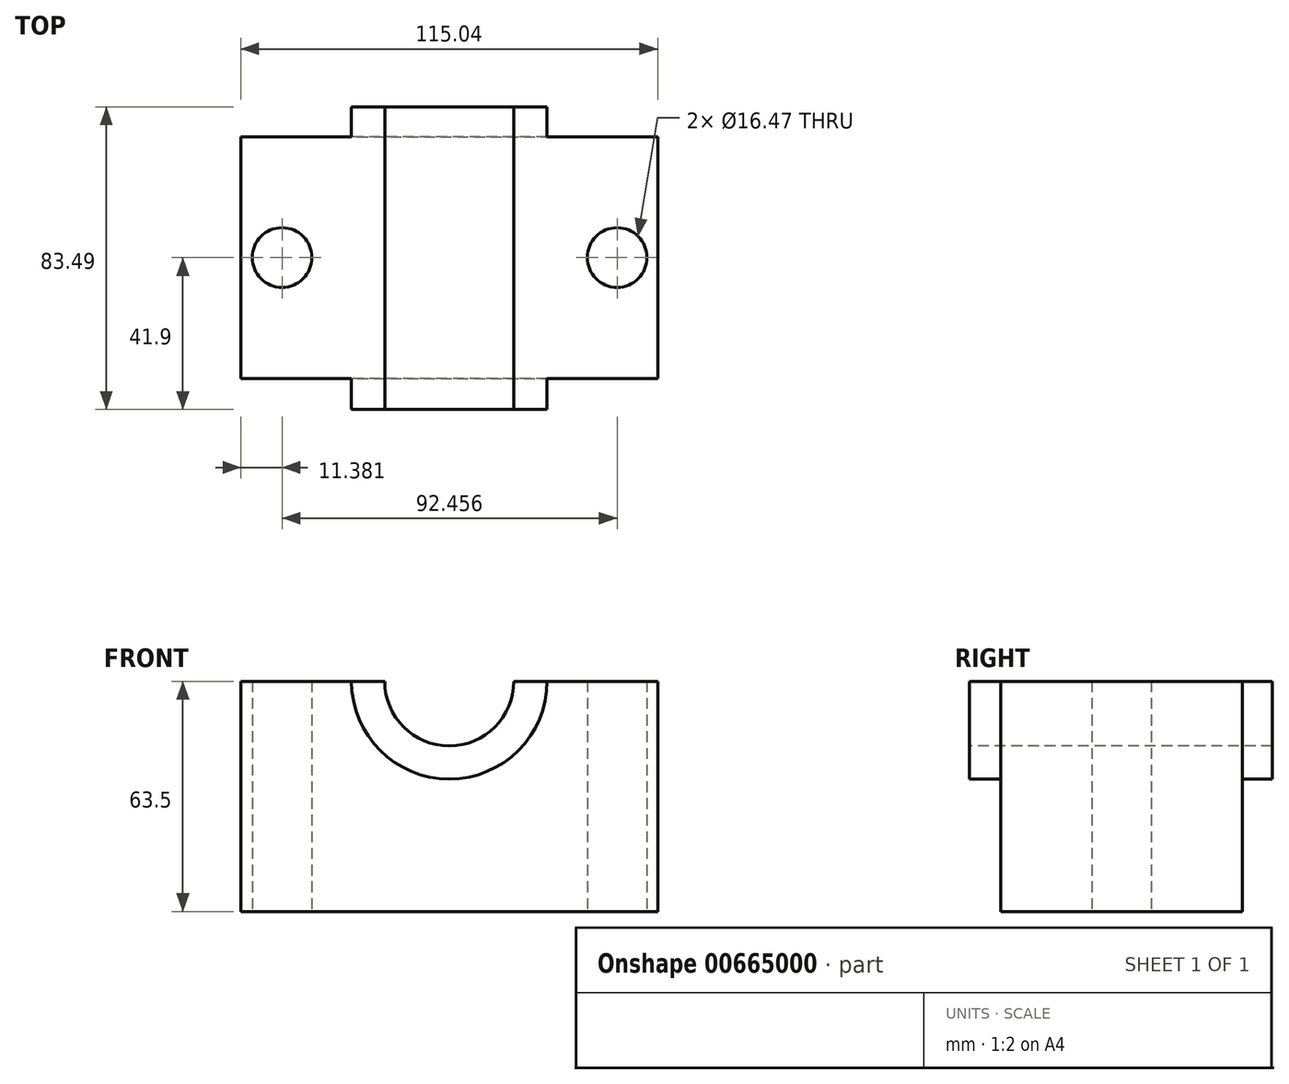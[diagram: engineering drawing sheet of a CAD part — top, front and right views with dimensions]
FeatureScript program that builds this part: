
annotation { "Feature Type Name" : "Feature", "Feature Type Description" : "" }
export const myFeature = defineFeature(function(context is Context, id is Id, definition is map)
    precondition{}
    {
        {
            var Q0;
            Q0=qCreatedBy(makeId("Top.planeOp"),FACE);
            var sketch = newSketch(context, id + "F0", { "sketchPlane" : qUnion([Q0])});
            skLineSegment(sketch, "E0.bottom", {"start": v(-57.52, 33.34) * mm, "end": v(57.52, 33.34) * mm});
            skLineSegment(sketch, "E0.top", {"start": v(-57.52, -33.34) * mm, "end": v(57.52, -33.34) * mm});
            skLineSegment(sketch, "E0.left", {"start": v(-57.52, 33.34) * mm, "end": v(-57.52, -33.34) * mm});
            skLineSegment(sketch, "E0.right", {"start": v(57.52, 33.34) * mm, "end": v(57.52, -33.34) * mm});
            skPoint(sketch, "E0.middle", {"position": v(0, 0) * mm});
            skCircle(sketch, "E1", {"center": v(-46.14, 0) * mm, "radius": 8.24 * mm});
            skCircle(sketch, "E2", {"center": v(46.32, 0) * mm, "radius": 8.24 * mm});
            skSolve(sketch);
        }
        {
            var Q0;
            Q0=makeQuery(id+"F0.imprint","IMPRINT",FACE,{"disambiguationData":[TD([[makeQuery(id+"F0.imprint","IMPRINT",EDGE,{"derivedFrom":sQuery(id+"F0.wireOp",EDGE,"E0.bottom")}),-1.0]])]});
            extrude(context, id + "F1", {"entities" : qUnion([Q0]), "depth" : 63.5 * mm, "offsetDistance" : 25.4 * mm});
        }
        {
            var Q0;
            Q0=makeQuery(id+"F1.opExtrude","SWEPT_FACE",FACE,{"disambiguationData":[OSD([sQuery(id+"F0.wireOp",EDGE,"E0.top")])]});
            var sketch = newSketch(context, id + "F2", { "sketchPlane" : qUnion([Q0])});
            skArc(sketch, "E3", {"start": v(-17.81, 63.5) * mm, "mid": v(0, 45.69) * mm, "end": v(17.81, 63.5) * mm});
            skLineSegment(sketch, "E4", {"start": v(-57.52, 63.5) * mm, "end": v(57.52, 63.5) * mm});
            skSolve(sketch);
        }
        {
            var Q0;
            {var subQ0=sQuery(id+"F2.wireOp",EDGE,"E3");var subQ1=makeQuery(id+"F1.opExtrude","CAP_EDGE",EDGE,{"disambiguationData":[OSD([sQuery(id+"F0.wireOp",EDGE,"E0.top")])],"isStart":false});var subQ2=makeQuery(id+"F2.imprint","INTERSECT",VERTEX,{"disambiguationData":[OD(0.0)],"derivedFrom":[subQ1,subQ0]});Q0=makeQuery(id+"F2.imprint","IMPRINT",FACE,{"disambiguationData":[TD([[makeQuery(id+"F2.imprint","IMPRINT",EDGE,{"disambiguationData":[TD([[subQ2,-1.0]])],"derivedFrom":subQ0}),1.0]])]});}
            extrude(context, id + "F3", {"entities" : qUnion([Q0]), "operationType" : NewBodyOperationType.REMOVE, "oppositeDirection" : true, "depth" : 76.2 * mm, "offsetDistance" : 25.4 * mm});
        }
        {
            var Q0;
            Q0=makeQuery(id+"F1.opExtrude","SWEPT_FACE",FACE,{"disambiguationData":[OSD([sQuery(id+"F0.wireOp",EDGE,"E0.top")])]});
            var sketch = newSketch(context, id + "F4", { "sketchPlane" : qUnion([Q0])});
            skArc(sketch, "E5", {"start": v(-26.98, 63.5) * mm, "mid": v(0, 36.52) * mm, "end": v(26.98, 63.5) * mm});
            skSolve(sketch);
        }
        {
            var Q0;
            Q0 = qSketchRegion(id + "F4", true);
            var Q1;
            {var subQ0=sQuery(id+"F4.wireOp",EDGE,"E5");Q1=makeQuery(id+"F4.imprint","IMPRINT",FACE,{"disambiguationData":[TD([[makeQuery(id+"F4.imprint","IMPRINT",EDGE,{"derivedFrom":subQ0}),1.0]])]});}
            extrude(context, id + "F5", {"entities" : qUnion([Q0, Q1]), "operationType" : NewBodyOperationType.ADD, "endBound" : BoundingType.SYMMETRIC, "depth" : 149.86 * mm, "offsetDistance" : 25.4 * mm});
        }
        {
            var Q0;
            Q0=qCreatedBy(makeId("Right.planeOp"),FACE);
            var sketch = newSketch(context, id + "F6", { "sketchPlane" : qUnion([Q0])});
            skLineSegment(sketch, "E6", {"start": v(-41.9, 63.74) * mm, "end": v(-41.9, 31.74) * mm});
            skLineSegment(sketch, "E7", {"start": v(-41.9, 31.74) * mm, "end": v(-124.58, 31.74) * mm});
            skLineSegment(sketch, "E8", {"start": v(-124.58, 31.74) * mm, "end": v(-124.58, 69.96) * mm});
            skLineSegment(sketch, "E9", {"start": v(-124.58, 69.96) * mm, "end": v(-41.9, 69.96) * mm});
            skLineSegment(sketch, "E10", {"start": v(-41.9, 69.96) * mm, "end": v(-41.9, 63.74) * mm});
            skSolve(sketch);
        }
        {
            var Q0;
            Q0 = qSketchRegion(id + "F6", true);
            extrude(context, id + "F7", {"entities" : qUnion([Q0]), "operationType" : NewBodyOperationType.REMOVE, "endBound" : BoundingType.SYMMETRIC, "oppositeDirection" : true, "depth" : 76.2 * mm, "offsetDistance" : 25.4 * mm});
        }
    });
